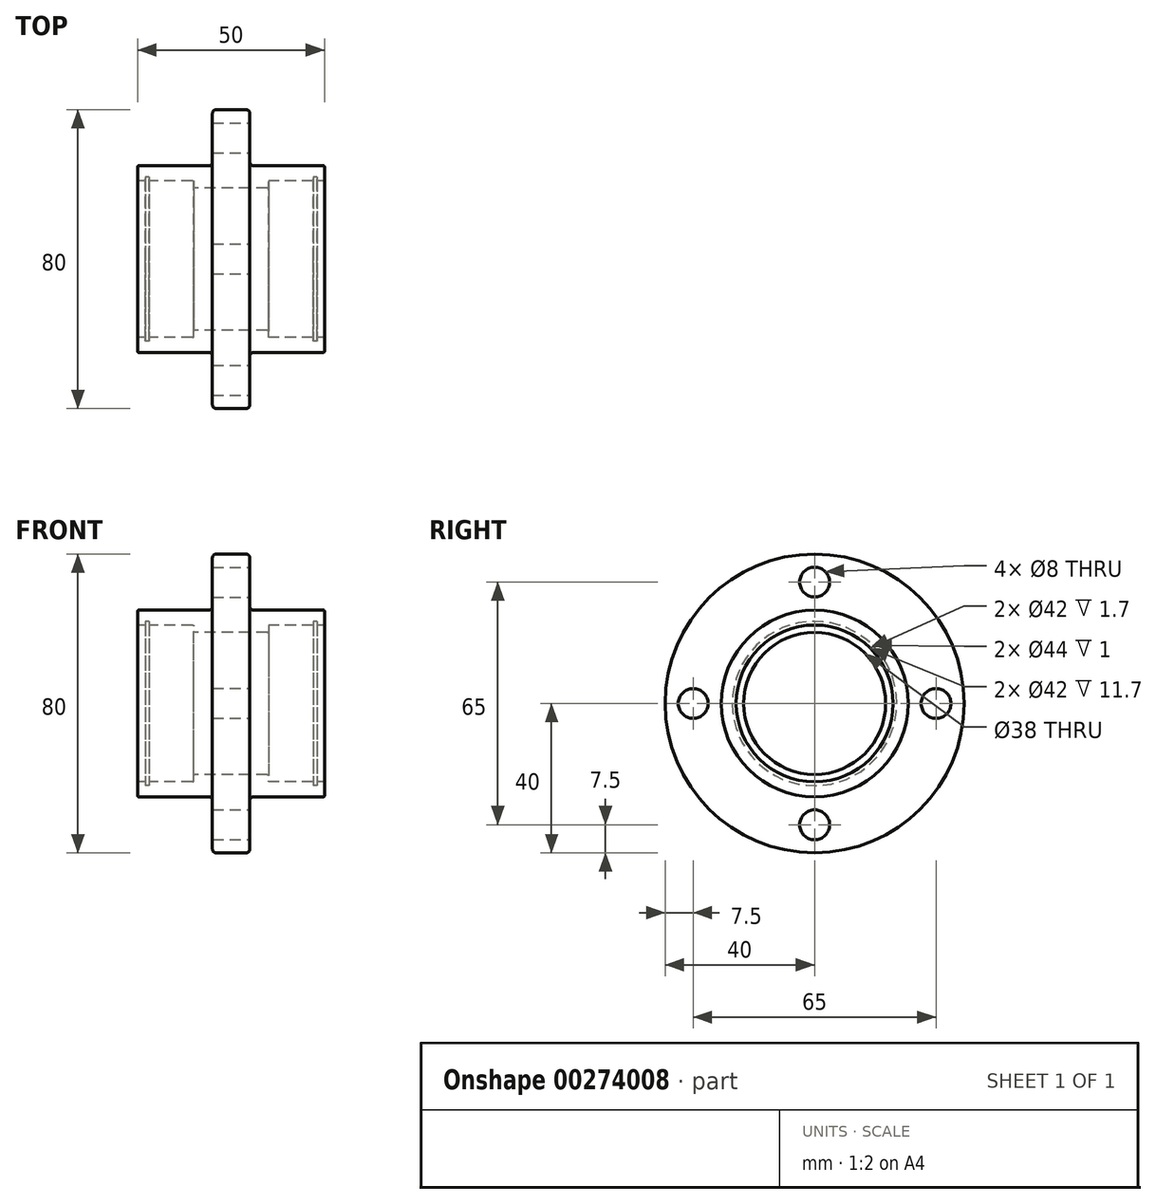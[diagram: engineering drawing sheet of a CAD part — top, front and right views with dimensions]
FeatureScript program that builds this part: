
annotation { "Feature Type Name" : "Feature", "Feature Type Description" : "" }
export const myFeature = defineFeature(function(context is Context, id is Id, definition is map)
    precondition{}
    {
        {
            var Q0;
            Q0=qCreatedBy(makeId("Front.planeOp"),FACE);
            var sketch = newSketch(context, id + "F0", { "sketchPlane" : qUnion([Q0])});
            skLineSegment(sketch, "E0", {"start": v(0, 0) * mm, "end": v(52.45, 0) * mm, "construction": true});
            skLineSegment(sketch, "E1", {"start": v(0, 21) * mm, "end": v(15, 21) * mm});
            skLineSegment(sketch, "E2", {"start": v(15, 21) * mm, "end": v(15, 19) * mm});
            skLineSegment(sketch, "E3", {"start": v(15, 19) * mm, "end": v(35, 19) * mm});
            skLineSegment(sketch, "E4", {"start": v(50, 21) * mm, "end": v(50, 25) * mm});
            skLineSegment(sketch, "E5", {"start": v(50, 25) * mm, "end": v(30, 25) * mm});
            skLineSegment(sketch, "E6", {"start": v(30, 25) * mm, "end": v(30, 40) * mm});
            skLineSegment(sketch, "E7", {"start": v(0, 25) * mm, "end": v(0, 21) * mm});
            skLineSegment(sketch, "E8.bottom", {"start": v(2, 21) * mm, "end": v(3, 21) * mm});
            skLineSegment(sketch, "E8.top", {"start": v(2, 22) * mm, "end": v(3, 22) * mm});
            skLineSegment(sketch, "E8.left", {"start": v(2, 21) * mm, "end": v(2, 22) * mm});
            skLineSegment(sketch, "E8.right", {"start": v(3, 21) * mm, "end": v(3, 22) * mm});
            skLineSegment(sketch, "E9", {"start": v(0, 25) * mm, "end": v(20, 25) * mm});
            skLineSegment(sketch, "E10", {"start": v(20, 25) * mm, "end": v(20, 40) * mm});
            skLineSegment(sketch, "E11", {"start": v(20, 40) * mm, "end": v(30, 40) * mm});
            skLineSegment(sketch, "E12", {"start": v(35, 19) * mm, "end": v(35, 21) * mm});
            skLineSegment(sketch, "E13", {"start": v(35, 21) * mm, "end": v(50, 21) * mm});
            skLineSegment(sketch, "E14.bottom", {"start": v(47, 21) * mm, "end": v(48, 21) * mm});
            skLineSegment(sketch, "E14.top", {"start": v(47, 22) * mm, "end": v(48, 22) * mm});
            skLineSegment(sketch, "E14.left", {"start": v(47, 21) * mm, "end": v(47, 22) * mm});
            skLineSegment(sketch, "E14.right", {"start": v(48, 21) * mm, "end": v(48, 22) * mm});
            skSolve(sketch);
        }
        {
            var Q0;
            {var subQ4=sQuery(id+"F0.wireOp",EDGE,"E2");Q0=makeQuery(id+"F0.imprint","IMPRINT",FACE,{"disambiguationData":[TD([[makeQuery(id+"F0.imprint","IMPRINT",EDGE,{"derivedFrom":subQ4}),1.0]])]});}
            var Q1;
            Q1=sQuery(id+"F0.wireOp",EDGE,"E0");
            revolve(context, id + "F1", {"entities" : qUnion([Q0]), "axis" : qUnion([Q1]), "revolveType" : RevolveType.FULL});
        }
        {
            var Q0;
            Q0=makeQuery(id+"F1.opRevolve","SWEPT_EDGE",EDGE,{"disambiguationData":[OSD([sQuery(id+"F0.wireOp",EDGE,"E1"),sQuery(id+"F0.wireOp",EDGE,"E2")])]});
            var Q1;
            Q1=makeQuery(id+"F1.opRevolve","SWEPT_EDGE",EDGE,{"disambiguationData":[OSD([sQuery(id+"F0.wireOp",EDGE,"E1"),sQuery(id+"F0.wireOp",EDGE,"E7")])]});
            var Q2;
            Q2=makeQuery(id+"F1.opRevolve","SWEPT_EDGE",EDGE,{"disambiguationData":[OSD([sQuery(id+"F0.wireOp",EDGE,"E2"),sQuery(id+"F0.wireOp",EDGE,"E3")])]});
            var Q3;
            Q3=makeQuery(id+"F1.opRevolve","SWEPT_EDGE",EDGE,{"disambiguationData":[OSD([sQuery(id+"F0.wireOp",EDGE,"E3"),sQuery(id+"F0.wireOp",EDGE,"E4")])]});
            var Q4;
            Q4=makeQuery(id+"F1.opRevolve","SWEPT_EDGE",EDGE,{"disambiguationData":[OSD([sQuery(id+"F0.wireOp",EDGE,"E12"),sQuery(id+"F0.wireOp",EDGE,"E13")])]});
            var Q5;
            Q5=makeQuery(id+"F1.opRevolve","SWEPT_EDGE",EDGE,{"disambiguationData":[OSD([sQuery(id+"F0.wireOp",EDGE,"E7"),sQuery(id+"F0.wireOp",EDGE,"E9")])]});
            fillet(context, id + "F2", {"entities" : qUnion([Q0, Q1, Q2, Q3, Q4, Q5]), "radius" : 0.3 * mm, "tangentPropagation" : true, "allowEdgeOverflow" : false});
        }
        {
            var Q0;
            Q0=makeQuery(id+"F1.opRevolve","SWEPT_EDGE",EDGE,{"disambiguationData":[OSD([sQuery(id+"F0.wireOp",EDGE,"E4"),sQuery(id+"F0.wireOp",EDGE,"E5")])]});
            var Q1;
            Q1=makeQuery(id+"F1.opRevolve","SWEPT_EDGE",EDGE,{"disambiguationData":[OSD([sQuery(id+"F0.wireOp",EDGE,"E5"),sQuery(id+"F0.wireOp",EDGE,"E6")])]});
            var Q2;
            Q2=makeQuery(id+"F1.opRevolve","SWEPT_EDGE",EDGE,{"disambiguationData":[OSD([sQuery(id+"F0.wireOp",EDGE,"E6"),sQuery(id+"F0.wireOp",EDGE,"8emcx9UW-5Iw0-E7Tb-gsbx-hsyMrdxOOZ0F")])]});
            var Q3;
            Q3=makeQuery(id+"F1.opRevolve","SWEPT_EDGE",EDGE,{"disambiguationData":[OSD([sQuery(id+"F0.wireOp",EDGE,"8emcx9UW-5Iw0-E7Tb-gsbx-hsyMrdxOOZ0F"),sQuery(id+"F0.wireOp",EDGE,"E7")])]});
            var Q4;
            Q4=makeQuery(id+"F1.opRevolve","SWEPT_EDGE",EDGE,{"disambiguationData":[OSD([sQuery(id+"F0.wireOp",EDGE,"E10"),sQuery(id+"F0.wireOp",EDGE,"E11")])]});
            var Q5;
            Q5=makeQuery(id+"F1.opRevolve","SWEPT_EDGE",EDGE,{"disambiguationData":[OSD([sQuery(id+"F0.wireOp",EDGE,"E9"),sQuery(id+"F0.wireOp",EDGE,"E10")])]});
            fillet(context, id + "F3", {"entities" : qUnion([Q0, Q1, Q2, Q3, Q4, Q5]), "radius" : 1 * mm, "tangentPropagation" : true, "allowEdgeOverflow" : false});
        }
        {
            var Q0;
            Q0=makeQuery(id+"F1.opRevolve","SWEPT_FACE",FACE,{"disambiguationData":[OSD([sQuery(id+"F0.wireOp",EDGE,"E6")])]});
            var sketch = newSketch(context, id + "F4", { "sketchPlane" : qUnion([Q0])});
            skCircle(sketch, "E15", {"center": v(0, 0) * mm, "radius": 32.5 * mm, "construction": true});
            skCircle(sketch, "E16", {"center": v(0, 32.5) * mm, "radius": 4 * mm});
            skCircle(sketch, "E17.1.0", {"center": v(-32.5, 0) * mm, "radius": 4 * mm});
            skCircle(sketch, "E17.2.0", {"center": v(0, -32.5) * mm, "radius": 4 * mm});
            skCircle(sketch, "E17.3.0", {"center": v(32.5, 0) * mm, "radius": 4 * mm});
            skSolve(sketch);
        }
        {
            var Q0;
            Q0=qSketchRegion(id+"F4",true);
            extrude(context, id + "F5", {"entities" : qUnion([Q0]), "operationType" : NewBodyOperationType.REMOVE, "endBound" : BoundingType.THROUGH_ALL, "oppositeDirection" : true, "depth" : 25 * mm});
        }
    });
